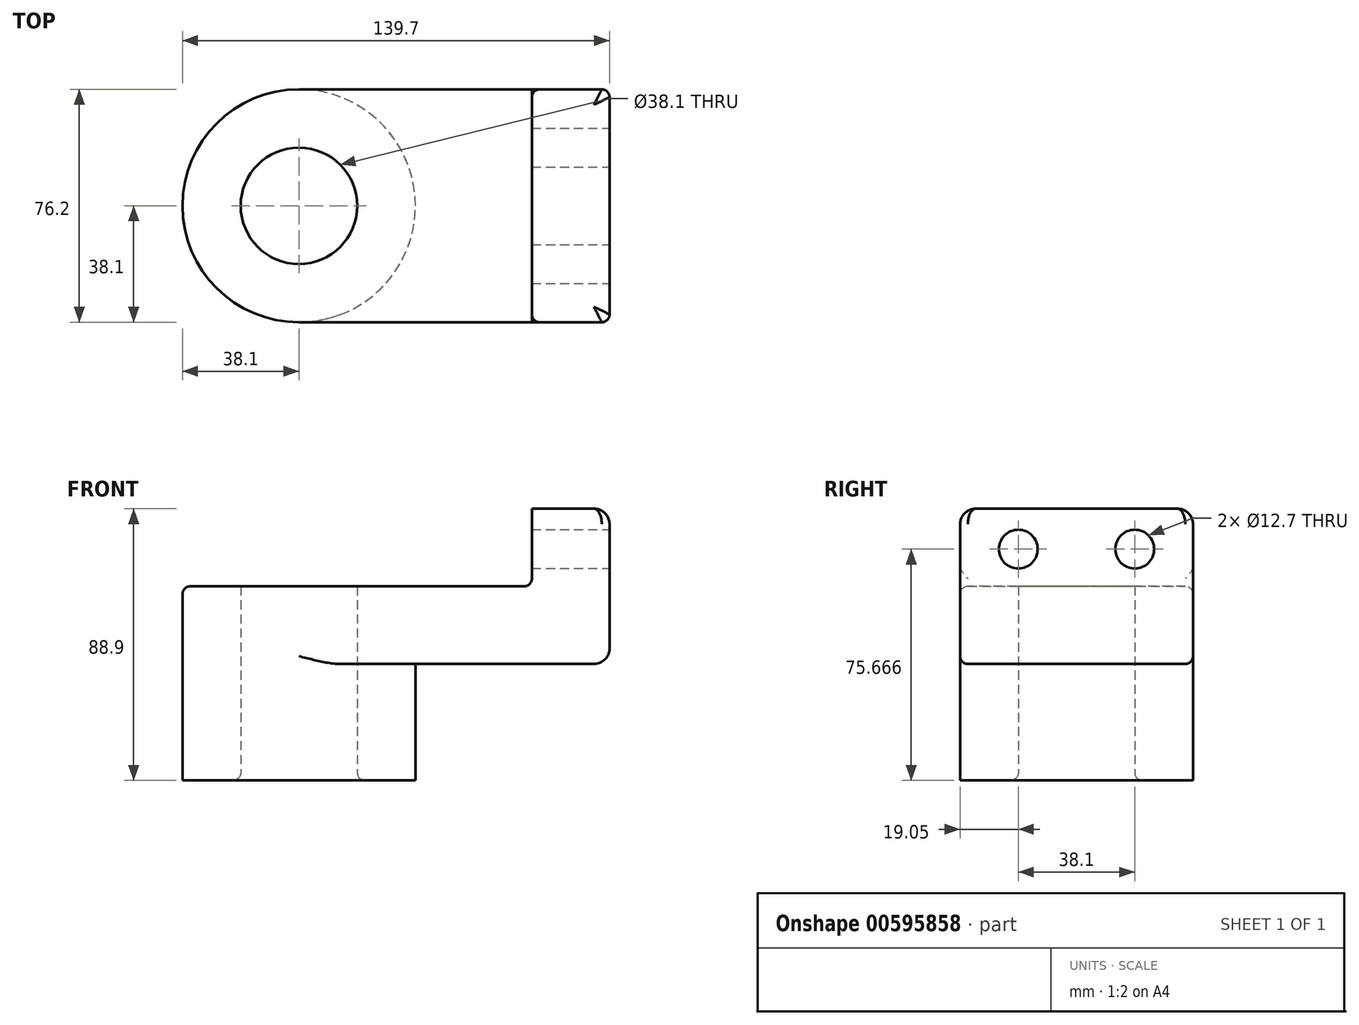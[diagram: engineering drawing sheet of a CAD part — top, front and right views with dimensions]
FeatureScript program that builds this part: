
annotation { "Feature Type Name" : "Feature", "Feature Type Description" : "" }
export const myFeature = defineFeature(function(context is Context, id is Id, definition is map)
    precondition{}
    {
        {
            var Q0;
            Q0=qCreatedBy(makeId("Top.planeOp"),FACE);
            var sketch = newSketch(context, id + "F0", { "sketchPlane" : qUnion([Q0])});
            skLineSegment(sketch, "E0.bottom", {"start": v(-50.8, -38.1) * mm, "end": v(50.8, -38.1) * mm});
            skLineSegment(sketch, "E0.top", {"start": v(-50.8, 38.1) * mm, "end": v(50.8, 38.1) * mm});
            skLineSegment(sketch, "E0.left", {"start": v(-50.8, 38.1) * mm, "end": v(-50.8, -38.1) * mm});
            skLineSegment(sketch, "E0.right", {"start": v(50.8, 38.1) * mm, "end": v(50.8, -38.1) * mm});
            skPoint(sketch, "E0.middle", {"position": v(0, 0) * mm});
            skCircle(sketch, "E1", {"center": v(-50.8, 0) * mm, "radius": 38.1 * mm});
            skCircle(sketch, "E2", {"center": v(-50.8, 0) * mm, "radius": 19.05 * mm});
            skSolve(sketch);
        }
        {
            var Q0;
            Q0 = qSketchRegion(id + "F0", true);
            extrude(context, id + "F1", {"entities" : qUnion([Q0]), "depth" : 25.4 * mm, "offsetDistance" : 25.4 * mm});
        }
        {
            var Q0;
            {var subQ1=sQuery(id+"F0.wireOp",EDGE,"E0.left");var subQ3=sQuery(id+"F0.wireOp",EDGE,"E2");var subQ4=makeQuery(id+"F0.imprint","INTERSECT",VERTEX,{"disambiguationData":[OD(0.0)],"derivedFrom":[subQ1,subQ3]});Q0=makeQuery(id+"F0.imprint","IMPRINT",FACE,{"disambiguationData":[TD([[makeQuery(id+"F0.imprint","IMPRINT",EDGE,{"disambiguationData":[TD([[subQ4,-1.0]])],"derivedFrom":subQ3}),-1.0]])]});}
            var Q1;
            {var subQ1=sQuery(id+"F0.wireOp",EDGE,"E0.left");var subQ3=sQuery(id+"F0.wireOp",EDGE,"E2");var subQ4=makeQuery(id+"F0.imprint","INTERSECT",VERTEX,{"disambiguationData":[OD(0.0)],"derivedFrom":[subQ1,subQ3]});Q1=makeQuery(id+"F0.imprint","IMPRINT",FACE,{"disambiguationData":[TD([[makeQuery(id+"F0.imprint","IMPRINT",EDGE,{"disambiguationData":[TD([[subQ4,1.0]])],"derivedFrom":subQ3}),-1.0]])]});}
            var Q2;
            Q2 = qSketchRegion(id + "F3", true);
            extrude(context, id + "F2", {"entities" : qUnion([Q0, Q1, Q2]), "operationType" : NewBodyOperationType.ADD, "oppositeDirection" : true, "depth" : 38.1 * mm, "offsetDistance" : 25.4 * mm});
        }
        {
            var Q0;
            Q0=makeQuery(id+"F1.opExtrude","SWEPT_FACE",FACE,{"disambiguationData":[OSD([sQuery(id+"F0.wireOp",EDGE,"E0.right")])]});
            var sketch = newSketch(context, id + "F3", { "sketchPlane" : qUnion([Q0])});
            skLineSegment(sketch, "E3.bottom", {"start": v(38.1, 0) * mm, "end": v(-38.1, 0) * mm});
            skLineSegment(sketch, "E3.top", {"start": v(38.1, 50.8) * mm, "end": v(-38.1, 50.8) * mm});
            skLineSegment(sketch, "E3.left", {"start": v(38.1, 0) * mm, "end": v(38.1, 50.8) * mm});
            skLineSegment(sketch, "E3.right", {"start": v(-38.1, 0) * mm, "end": v(-38.1, 50.8) * mm});
            skLineSegment(sketch, "E4.bottom", {"start": v(-38.1, 50.8) * mm, "end": v(-38.1, 50.8) * mm});
            skLineSegment(sketch, "E5", {"start": v(0, 25.4) * mm, "end": v(0, 50.8) * mm, "construction": true});
            skCircle(sketch, "E6", {"center": v(-19.05, 37.57) * mm, "radius": 6.35 * mm});
            skCircle(sketch, "E7.MirrorC", {"center": v(19.05, 37.57) * mm, "radius": 6.35 * mm});
            skSolve(sketch);
        }
        {
            var Q0;
            Q0 = qSketchRegion(id + "F3", true);
            extrude(context, id + "F4", {"entities" : qUnion([Q0]), "operationType" : NewBodyOperationType.ADD, "oppositeDirection" : true, "depth" : 25.4 * mm, "offsetDistance" : 25.4 * mm});
        }
        {
            var Q0;
            Q0=makeQuery(id+"F2.opExtrude","CAP_EDGE",EDGE,{"disambiguationData":[OSD([sQuery(id+"F0.wireOp",EDGE,"E1")])],"isStart":true});
            var Q1;
            Q1=makeQuery(id+"F1.opExtrude","CAP_EDGE",EDGE,{"disambiguationData":[OSD([sQuery(id+"F0.wireOp",EDGE,"E0.right")])],"isStart":true});
            var Q2;
            Q2=makeQuery(id+"F4.opExtrude","CAP_EDGE",EDGE,{"disambiguationData":[OSD([sQuery(id+"F3.wireOp",EDGE,"E3.top")])],"isStart":true});
            var Q3;
            Q3=makeQuery(id+"F4.opExtrude","SWEPT_EDGE",EDGE,{"disambiguationData":[OSD([sQuery(id+"F3.wireOp",EDGE,"E3.top"),sQuery(id+"F3.wireOp",EDGE,"E3.left")])]});
            var Q4;
            Q4=makeQuery(id+"F4.opExtrude","SWEPT_EDGE",EDGE,{"disambiguationData":[OSD([sQuery(id+"F3.wireOp",EDGE,"E3.top"),sQuery(id+"F3.wireOp",EDGE,"E3.right")])]});
            fillet(context, id + "F5", {"entities" : qUnion([Q0, Q1, Q2, Q3, Q4]), "radius" : 5.08 * mm, "tangentPropagation" : true, "allowEdgeOverflow" : false});
        }
        {
            var Q0;
            Q0=makeQuery(id+"F1.opExtrude","CAP_EDGE",EDGE,{"disambiguationData":[OSD([sQuery(id+"F0.wireOp",EDGE,"E0.top")])],"isStart":true});
            var Q1;
            Q1=makeQuery(id+"F1.opExtrude","CAP_EDGE",EDGE,{"disambiguationData":[OSD([sQuery(id+"F0.wireOp",EDGE,"E0.bottom")])],"isStart":true});
            var Q2;
            Q2=makeQuery(id+"F1.opExtrude","CAP_EDGE",EDGE,{"disambiguationData":[OSD([sQuery(id+"F0.wireOp",EDGE,"E0.top")])],"isStart":false});
            var Q3;
            Q3=makeQuery(id+"F4.boolean.opBoolean","INTERSECT",EDGE,{"derivedFrom":[makeQuery(id+"F1.opExtrude","CAP_FACE",FACE,{"disambiguationData":[OSD([sQuery(id+"F0.wireOp",EDGE,"E0.bottom"),sQuery(id+"F0.wireOp",EDGE,"E0.top"),sQuery(id+"F0.wireOp",EDGE,"E0.right"),sQuery(id+"F0.wireOp",EDGE,"E1"),sQuery(id+"F0.wireOp",EDGE,"E2")])],"isStart":false}),makeQuery(id+"F4.opExtrude","CAP_FACE",FACE,{"disambiguationData":[OSD([sQuery(id+"F3.wireOp",EDGE,"E3.bottom"),sQuery(id+"F3.wireOp",EDGE,"E3.top"),sQuery(id+"F3.wireOp",EDGE,"E3.left"),sQuery(id+"F3.wireOp",EDGE,"E3.right"),sQuery(id+"F3.wireOp",EDGE,"E6"),sQuery(id+"F3.wireOp",EDGE,"E7.MirrorC")])],"isStart":false})]});
            fillet(context, id + "F6", {"entities" : qUnion([Q0, Q1, Q2, Q3]), "radius" : 2.54 * mm, "tangentPropagation" : true, "allowEdgeOverflow" : false});
        }
        {
            var Q0;
            Q0=makeQuery(id+"F2.opExtrude","CAP_EDGE",EDGE,{"disambiguationData":[OSD([sQuery(id+"F0.wireOp",EDGE,"E2")])],"isStart":false});
            fillet(context, id + "F7", {"entities" : qUnion([Q0]), "radius" : 2.54 * mm, "tangentPropagation" : true, "allowEdgeOverflow" : false});
        }
    });
